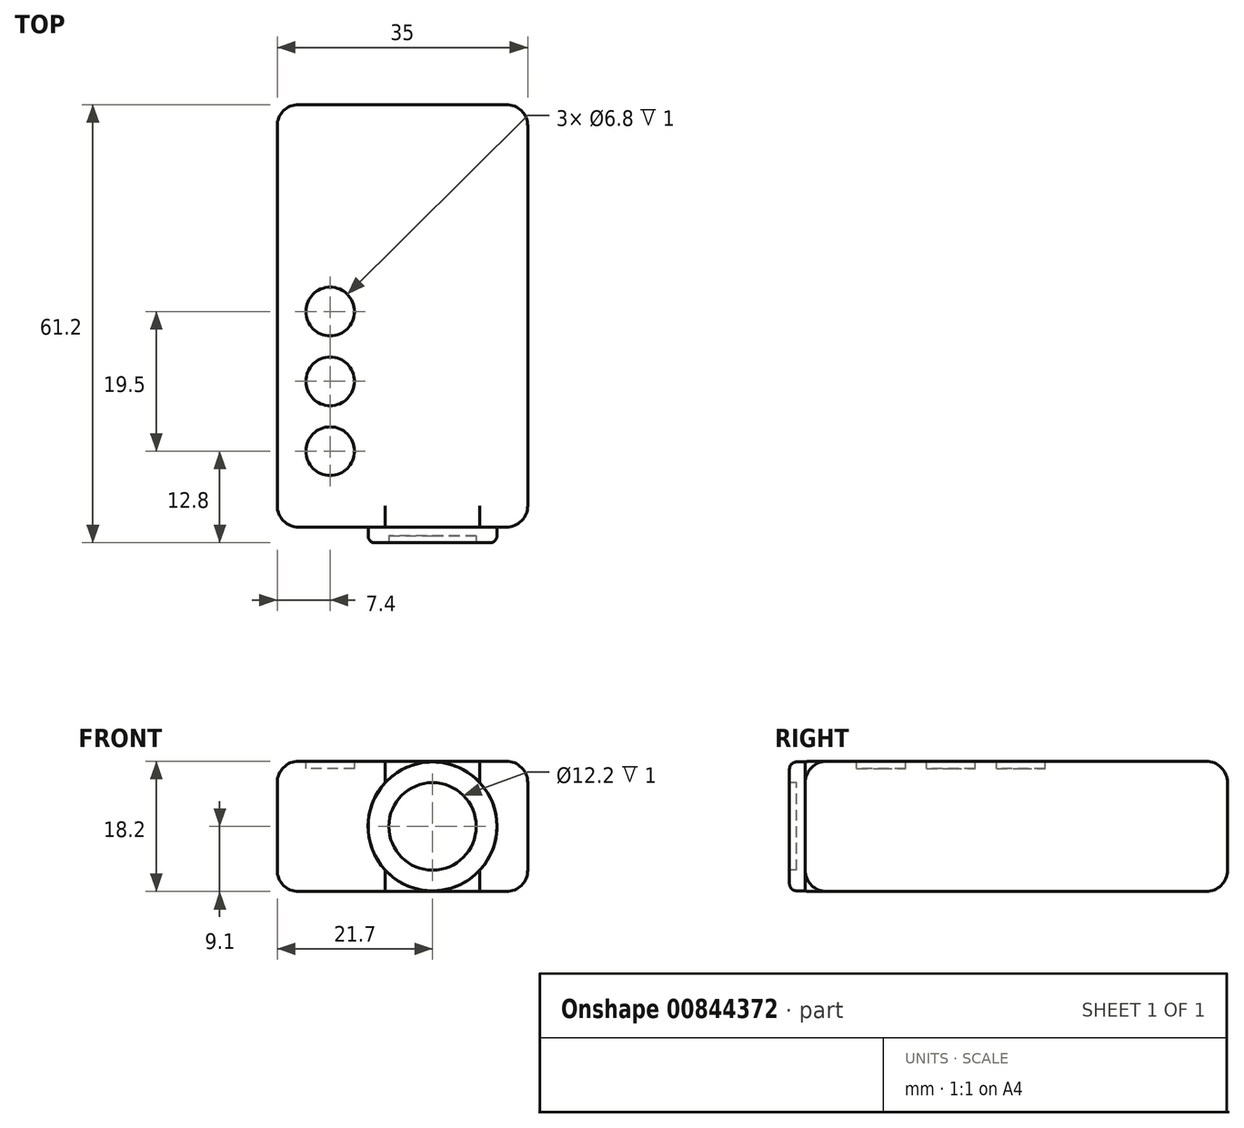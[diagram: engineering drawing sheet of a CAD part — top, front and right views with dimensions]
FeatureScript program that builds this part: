
annotation { "Feature Type Name" : "Feature", "Feature Type Description" : "" }
export const myFeature = defineFeature(function(context is Context, id is Id, definition is map)
    precondition{}
    {
        {
            var Q0;
            Q0=qCreatedBy(makeId("Top.planeOp"),FACE);
            var sketch = newSketch(context, id + "F0", { "sketchPlane" : qUnion([Q0])});
            skLineSegment(sketch, "E0.bottom", {"start": v(-35, 0) * mm, "end": v(0, 0) * mm});
            skLineSegment(sketch, "E0.top", {"start": v(-35, 59) * mm, "end": v(0, 59) * mm});
            skLineSegment(sketch, "E0.left", {"start": v(-35, 0) * mm, "end": v(-35, 59) * mm});
            skLineSegment(sketch, "E0.right", {"start": v(0, 0) * mm, "end": v(0, 59) * mm});
            skSolve(sketch);
        }
        {
            var Q0;
            Q0 = qSketchRegion(id + "F0", true);
            extrude(context, id + "F1", {"entities" : qUnion([Q0]), "depth" : 18.2 * mm, "offsetDistance" : 25 * mm});
        }
        {
            var Q0;
            Q0=makeQuery(id+"F1.opExtrude","SWEPT_FACE",FACE,{"disambiguationData":[OSD([sQuery(id+"F0.wireOp",EDGE,"E0.bottom")])]});
            var sketch = newSketch(context, id + "F2", { "sketchPlane" : qUnion([Q0])});
            skLineSegment(sketch, "E1", {"start": v(0, 9.1) * mm, "end": v(-35, 9.1) * mm, "construction": true});
            skCircle(sketch, "E2", {"center": v(-13.3, 9.1) * mm, "radius": 9 * mm});
            skSolve(sketch);
        }
        {
            var Q0;
            Q0 = qSketchRegion(id + "F2", true);
            extrude(context, id + "F3", {"entities" : qUnion([Q0]), "operationType" : NewBodyOperationType.ADD, "depth" : 2.2 * mm, "offsetDistance" : 25 * mm});
        }
        {
            var Q0;
            Q0=makeQuery(id+"F3.opExtrude","CAP_FACE",FACE,{"disambiguationData":[OSD([sQuery(id+"F2.wireOp",EDGE,"E2")])],"isStart":false});
            var sketch = newSketch(context, id + "F4", { "sketchPlane" : qUnion([Q0])});
            skCircle(sketch, "E3", {"center": v(-13.3, 9.1) * mm, "radius": 6.1 * mm});
            skSolve(sketch);
        }
        {
            var Q0;
            Q0 = qSketchRegion(id + "F4", true);
            extrude(context, id + "F5", {"entities" : qUnion([Q0]), "operationType" : NewBodyOperationType.REMOVE, "oppositeDirection" : true, "depth" : 1 * mm, "offsetDistance" : 25 * mm});
        }
        {
            var Q0;
            Q0=makeQuery(id+"F1.opExtrude","CAP_FACE",FACE,{"disambiguationData":[OSD([sQuery(id+"F0.wireOp",EDGE,"E0.bottom"),sQuery(id+"F0.wireOp",EDGE,"E0.top"),sQuery(id+"F0.wireOp",EDGE,"E0.left"),sQuery(id+"F0.wireOp",EDGE,"E0.right")])],"isStart":false});
            var sketch = newSketch(context, id + "F6", { "sketchPlane" : qUnion([Q0])});
            skCircle(sketch, "E4", {"center": v(-27.6, 10.6) * mm, "radius": 3.4 * mm});
            skLineSegment(sketch, "E5", {"start": v(-27.6, 0) * mm, "end": v(-27.6, 59) * mm, "construction": true});
            skCircle(sketch, "E6", {"center": v(-27.6, 20.35) * mm, "radius": 3.4 * mm});
            skCircle(sketch, "E7", {"center": v(-27.6, 30.1) * mm, "radius": 3.4 * mm});
            skSolve(sketch);
        }
        {
            var Q0;
            Q0 = qSketchRegion(id + "F6", true);
            extrude(context, id + "F7", {"entities" : qUnion([Q0]), "operationType" : NewBodyOperationType.REMOVE, "oppositeDirection" : true, "depth" : 1 * mm, "offsetDistance" : 25 * mm});
        }
        {
            var Q0;
            Q0=makeQuery(id+"F1.opExtrude","CAP_EDGE",EDGE,{"disambiguationData":[OSD([sQuery(id+"F0.wireOp",EDGE,"E0.right")])],"isStart":false});
            var Q1;
            Q1=makeQuery(id+"F1.opExtrude","CAP_EDGE",EDGE,{"disambiguationData":[OSD([sQuery(id+"F0.wireOp",EDGE,"E0.bottom")])],"isStart":false});
            var Q2;
            Q2=makeQuery(id+"F1.opExtrude","SWEPT_EDGE",EDGE,{"disambiguationData":[OSD([sQuery(id+"F0.wireOp",EDGE,"E0.bottom"),sQuery(id+"F0.wireOp",EDGE,"E0.right")])]});
            var Q3;
            Q3=makeQuery(id+"F1.opExtrude","CAP_EDGE",EDGE,{"disambiguationData":[OSD([sQuery(id+"F0.wireOp",EDGE,"E0.right")])],"isStart":true});
            var Q4;
            Q4=makeQuery(id+"F1.opExtrude","CAP_EDGE",EDGE,{"disambiguationData":[OSD([sQuery(id+"F0.wireOp",EDGE,"E0.bottom")])],"isStart":true});
            var Q5;
            Q5=makeQuery(id+"F1.opExtrude","SWEPT_EDGE",EDGE,{"disambiguationData":[OSD([sQuery(id+"F0.wireOp",EDGE,"E0.bottom"),sQuery(id+"F0.wireOp",EDGE,"E0.left")])]});
            var Q6;
            Q6=makeQuery(id+"F1.opExtrude","CAP_EDGE",EDGE,{"disambiguationData":[OSD([sQuery(id+"F0.wireOp",EDGE,"E0.left")])],"isStart":false});
            var Q7;
            Q7=makeQuery(id+"F1.opExtrude","CAP_EDGE",EDGE,{"disambiguationData":[OSD([sQuery(id+"F0.wireOp",EDGE,"E0.top")])],"isStart":false});
            var Q8;
            Q8=makeQuery(id+"F1.opExtrude","SWEPT_EDGE",EDGE,{"disambiguationData":[OSD([sQuery(id+"F0.wireOp",EDGE,"E0.top"),sQuery(id+"F0.wireOp",EDGE,"E0.right")])]});
            var Q9;
            Q9=makeQuery(id+"F1.opExtrude","CAP_EDGE",EDGE,{"disambiguationData":[OSD([sQuery(id+"F0.wireOp",EDGE,"E0.top")])],"isStart":true});
            var Q10;
            Q10=makeQuery(id+"F1.opExtrude","SWEPT_EDGE",EDGE,{"disambiguationData":[OSD([sQuery(id+"F0.wireOp",EDGE,"E0.top"),sQuery(id+"F0.wireOp",EDGE,"E0.left")])]});
            var Q11;
            Q11=makeQuery(id+"F1.opExtrude","CAP_EDGE",EDGE,{"disambiguationData":[OSD([sQuery(id+"F0.wireOp",EDGE,"E0.left")])],"isStart":true});
            fillet(context, id + "F8", {"entities" : qUnion([Q0, Q1, Q2, Q3, Q4, Q5, Q6, Q7, Q8, Q9, Q10, Q11]), "radius" : 3 * mm, "tangentPropagation" : true, "allowEdgeOverflow" : false});
        }
        {
            var Q0;
            Q0=makeQuery(id+"F3.opExtrude","CAP_EDGE",EDGE,{"disambiguationData":[OSD([sQuery(id+"F2.wireOp",EDGE,"E2")])],"isStart":false});
            var Q1;
            Q1=makeQuery(id+"F5.boolean.opBoolean","COPY",EDGE,{"derivedFrom":makeQuery(id+"F5.opExtrude","CAP_EDGE",EDGE,{"disambiguationData":[OSD([sQuery(id+"F4.wireOp",EDGE,"E3")])],"isStart":true})});
            fillet(context, id + "F9", {"entities" : qUnion([Q0, Q1]), "radius" : 1 * mm, "tangentPropagation" : true, "allowEdgeOverflow" : false});
        }
    });
